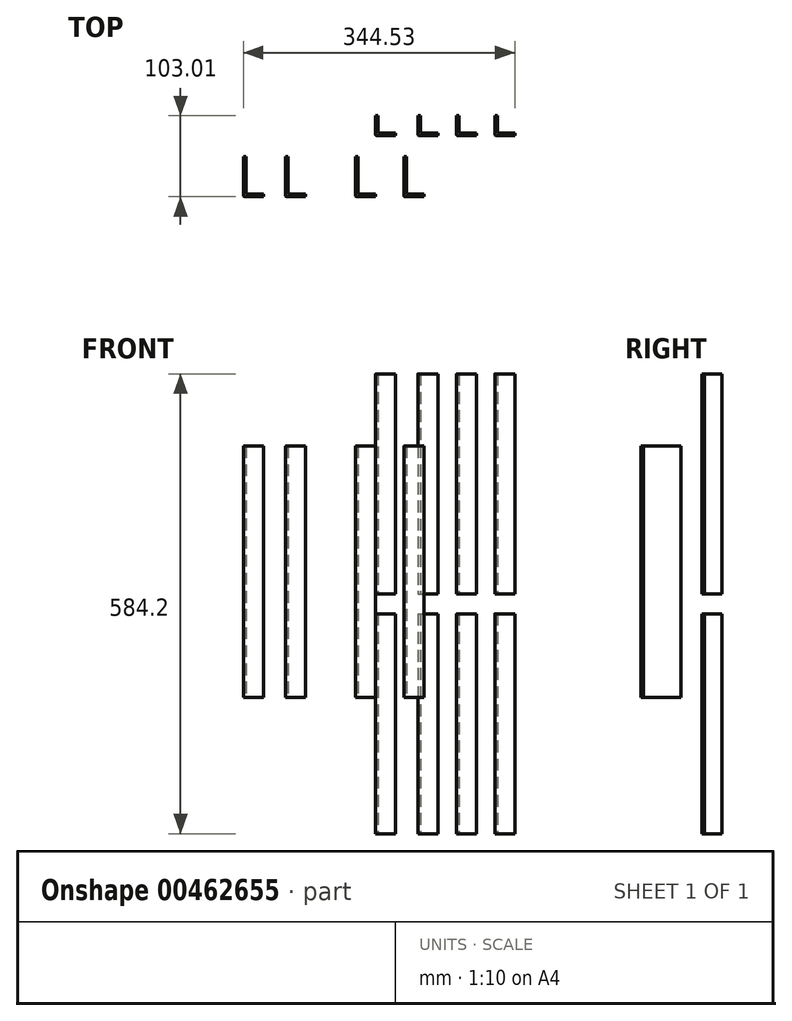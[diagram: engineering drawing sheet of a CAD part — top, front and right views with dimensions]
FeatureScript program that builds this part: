
annotation { "Feature Type Name" : "Feature", "Feature Type Description" : "" }
export const myFeature = defineFeature(function(context is Context, id is Id, definition is map)
    precondition{}
    {
        {
            var Q0;
            Q0=qCreatedBy(makeId("Top.planeOp"),FACE);
            var sketch = newSketch(context, id + "F0", { "sketchPlane" : qUnion([Q0])});
            skLineSegment(sketch, "E0", {"start": v(-52.96, 48.73) * mm, "end": v(-52.96, 24.92) * mm});
            skLineSegment(sketch, "E1", {"start": v(-51.37, 23.33) * mm, "end": v(-27.56, 23.33) * mm});
            skLineSegment(sketch, "E2", {"start": v(-27.56, 23.33) * mm, "end": v(-27.56, 26.5) * mm});
            skLineSegment(sketch, "E3", {"start": v(-27.56, 26.5) * mm, "end": v(-49.79, 26.5) * mm});
            skLineSegment(sketch, "E4", {"start": v(-52.96, 48.73) * mm, "end": v(-49.79, 48.73) * mm});
            skLineSegment(sketch, "E5", {"start": v(-49.79, 48.73) * mm, "end": v(-49.79, 26.5) * mm});
            skPoint(sketch, "E6.visualSharp", {"position": v(-52.96, 48.73) * mm});
            skPoint(sketch, "E7.visualSharp", {"position": v(-52.96, 23.33) * mm});
            skArc(sketch, "E7.filletArc", {"start": v(-52.96, 24.92) * mm, "mid": v(-52.5, 23.8) * mm, "end": v(-51.37, 23.33) * mm});
            skSolve(sketch);
        }
        {
            var Q0;
            Q0=makeQuery(id+"F0.imprint","IMPRINT",FACE,{"disambiguationData":[TD([[makeQuery(id+"F0.imprint","IMPRINT",EDGE,{"derivedFrom":sQuery(id+"F0.wireOp",EDGE,"E0")}),1.0]])]});
            extrude(context, id + "F1", {"entities" : qUnion([Q0]), "depth" : 279.4 * mm, "symmetric" : true});
        }
        {
            var Q0;
            Q0=makeQuery(id+"F1.opExtrude","SWEPT_BODY",BODY,{"disambiguationData":[OSD([sQuery(id+"F0.wireOp",EDGE,"E0"),sQuery(id+"F0.wireOp",EDGE,"E1"),sQuery(id+"F0.wireOp",EDGE,"E2"),sQuery(id+"F0.wireOp",EDGE,"E3"),sQuery(id+"F0.wireOp",EDGE,"E4"),sQuery(id+"F0.wireOp",EDGE,"E5"),sQuery(id+"F0.wireOp",EDGE,"E7.filletArc")])]});
            transform(context, id + "F2", {"entities" : qUnion([Q0]), "transformType" : TransformType.TRANSLATION_3D, "dx" : 53.6 * mm, "dy" : 0 * mm, "dz" : 0 * mm, "makeCopy" : true});
        }
        {
            var Q0;
            Q0=makeQuery(id+"F2.opPattern","COPY",BODY,{"derivedFrom":makeQuery(id+"F1.opExtrude","SWEPT_BODY",BODY,{"disambiguationData":[OSD([sQuery(id+"F0.wireOp",EDGE,"E0"),sQuery(id+"F0.wireOp",EDGE,"E1"),sQuery(id+"F0.wireOp",EDGE,"E2"),sQuery(id+"F0.wireOp",EDGE,"E3"),sQuery(id+"F0.wireOp",EDGE,"E4"),sQuery(id+"F0.wireOp",EDGE,"E5"),sQuery(id+"F0.wireOp",EDGE,"E7.filletArc")])]}),"instanceName":"1"});
            transform(context, id + "F3", {"entities" : qUnion([Q0]), "transformType" : TransformType.TRANSLATION_3D, "dx" : 49.28 * mm, "dy" : 0 * mm, "dz" : 0 * mm, "makeCopy" : true});
        }
        {
            var Q0;
            Q0=makeQuery(id+"F2.opPattern","COPY",BODY,{"derivedFrom":makeQuery(id+"F1.opExtrude","SWEPT_BODY",BODY,{"disambiguationData":[OSD([sQuery(id+"F0.wireOp",EDGE,"E0"),sQuery(id+"F0.wireOp",EDGE,"E1"),sQuery(id+"F0.wireOp",EDGE,"E2"),sQuery(id+"F0.wireOp",EDGE,"E3"),sQuery(id+"F0.wireOp",EDGE,"E4"),sQuery(id+"F0.wireOp",EDGE,"E5"),sQuery(id+"F0.wireOp",EDGE,"E7.filletArc")])]}),"instanceName":"1"});
            transform(context, id + "F4", {"entities" : qUnion([Q0]), "transformType" : TransformType.TRANSLATION_3D, "dx" : 97.8 * mm, "dy" : 0 * mm, "dz" : 0 * mm, "makeCopy" : true});
        }
        {
            var Q0;
            Q0=makeQuery(id+"F1.opExtrude","SWEPT_BODY",BODY,{"disambiguationData":[OSD([sQuery(id+"F0.wireOp",EDGE,"E0"),sQuery(id+"F0.wireOp",EDGE,"E1"),sQuery(id+"F0.wireOp",EDGE,"E2"),sQuery(id+"F0.wireOp",EDGE,"E3"),sQuery(id+"F0.wireOp",EDGE,"E4"),sQuery(id+"F0.wireOp",EDGE,"E5"),sQuery(id+"F0.wireOp",EDGE,"E7.filletArc")])]});
            var Q1;
            Q1=makeQuery(id+"F2.opPattern","COPY",BODY,{"derivedFrom":makeQuery(id+"F1.opExtrude","SWEPT_BODY",BODY,{"disambiguationData":[OSD([sQuery(id+"F0.wireOp",EDGE,"E0"),sQuery(id+"F0.wireOp",EDGE,"E1"),sQuery(id+"F0.wireOp",EDGE,"E2"),sQuery(id+"F0.wireOp",EDGE,"E3"),sQuery(id+"F0.wireOp",EDGE,"E4"),sQuery(id+"F0.wireOp",EDGE,"E5"),sQuery(id+"F0.wireOp",EDGE,"E7.filletArc")])]}),"instanceName":"1"});
            var Q2;
            Q2=makeQuery(id+"F4.opPattern","COPY",BODY,{"derivedFrom":makeQuery(id+"F2.opPattern","COPY",BODY,{"derivedFrom":makeQuery(id+"F1.opExtrude","SWEPT_BODY",BODY,{"disambiguationData":[OSD([sQuery(id+"F0.wireOp",EDGE,"E0"),sQuery(id+"F0.wireOp",EDGE,"E1"),sQuery(id+"F0.wireOp",EDGE,"E2"),sQuery(id+"F0.wireOp",EDGE,"E3"),sQuery(id+"F0.wireOp",EDGE,"E4"),sQuery(id+"F0.wireOp",EDGE,"E5"),sQuery(id+"F0.wireOp",EDGE,"E7.filletArc")])]}),"instanceName":"1"}),"instanceName":"1"});
            var Q3;
            Q3=makeQuery(id+"F3.opPattern","COPY",BODY,{"derivedFrom":makeQuery(id+"F2.opPattern","COPY",BODY,{"derivedFrom":makeQuery(id+"F1.opExtrude","SWEPT_BODY",BODY,{"disambiguationData":[OSD([sQuery(id+"F0.wireOp",EDGE,"E0"),sQuery(id+"F0.wireOp",EDGE,"E1"),sQuery(id+"F0.wireOp",EDGE,"E2"),sQuery(id+"F0.wireOp",EDGE,"E3"),sQuery(id+"F0.wireOp",EDGE,"E4"),sQuery(id+"F0.wireOp",EDGE,"E5"),sQuery(id+"F0.wireOp",EDGE,"E7.filletArc")])]}),"instanceName":"1"}),"instanceName":"1"});
            transform(context, id + "F5", {"entities" : qUnion([Q0, Q1, Q2, Q3]), "transformType" : TransformType.TRANSLATION_3D, "dx" : 0 * mm, "dy" : 0 * mm, "dz" : -193.3 * mm, "makeCopy" : false});
        }
        {
            var Q0;
            Q0=makeQuery(id+"F1.opExtrude","SWEPT_BODY",BODY,{"disambiguationData":[OSD([sQuery(id+"F0.wireOp",EDGE,"E0"),sQuery(id+"F0.wireOp",EDGE,"E1"),sQuery(id+"F0.wireOp",EDGE,"E2"),sQuery(id+"F0.wireOp",EDGE,"E3"),sQuery(id+"F0.wireOp",EDGE,"E4"),sQuery(id+"F0.wireOp",EDGE,"E5"),sQuery(id+"F0.wireOp",EDGE,"E7.filletArc")])]});
            var Q1;
            Q1=makeQuery(id+"F2.opPattern","COPY",BODY,{"derivedFrom":makeQuery(id+"F1.opExtrude","SWEPT_BODY",BODY,{"disambiguationData":[OSD([sQuery(id+"F0.wireOp",EDGE,"E0"),sQuery(id+"F0.wireOp",EDGE,"E1"),sQuery(id+"F0.wireOp",EDGE,"E2"),sQuery(id+"F0.wireOp",EDGE,"E3"),sQuery(id+"F0.wireOp",EDGE,"E4"),sQuery(id+"F0.wireOp",EDGE,"E5"),sQuery(id+"F0.wireOp",EDGE,"E7.filletArc")])]}),"instanceName":"1"});
            var Q2;
            Q2=makeQuery(id+"F3.opPattern","COPY",BODY,{"derivedFrom":makeQuery(id+"F2.opPattern","COPY",BODY,{"derivedFrom":makeQuery(id+"F1.opExtrude","SWEPT_BODY",BODY,{"disambiguationData":[OSD([sQuery(id+"F0.wireOp",EDGE,"E0"),sQuery(id+"F0.wireOp",EDGE,"E1"),sQuery(id+"F0.wireOp",EDGE,"E2"),sQuery(id+"F0.wireOp",EDGE,"E3"),sQuery(id+"F0.wireOp",EDGE,"E4"),sQuery(id+"F0.wireOp",EDGE,"E5"),sQuery(id+"F0.wireOp",EDGE,"E7.filletArc")])]}),"instanceName":"1"}),"instanceName":"1"});
            var Q3;
            Q3=makeQuery(id+"F4.opPattern","COPY",BODY,{"derivedFrom":makeQuery(id+"F2.opPattern","COPY",BODY,{"derivedFrom":makeQuery(id+"F1.opExtrude","SWEPT_BODY",BODY,{"disambiguationData":[OSD([sQuery(id+"F0.wireOp",EDGE,"E0"),sQuery(id+"F0.wireOp",EDGE,"E1"),sQuery(id+"F0.wireOp",EDGE,"E2"),sQuery(id+"F0.wireOp",EDGE,"E3"),sQuery(id+"F0.wireOp",EDGE,"E4"),sQuery(id+"F0.wireOp",EDGE,"E5"),sQuery(id+"F0.wireOp",EDGE,"E7.filletArc")])]}),"instanceName":"1"}),"instanceName":"1"});
            transform(context, id + "F6", {"entities" : qUnion([Q0, Q1, Q2, Q3]), "transformType" : TransformType.TRANSLATION_3D, "dx" : 0 * mm, "dy" : 0 * mm, "dz" : 304.8 * mm, "makeCopy" : true});
        }
        {
            var Q0;
            Q0=qCreatedBy(makeId("Top.planeOp"),FACE);
            var sketch = newSketch(context, id + "F7", { "sketchPlane" : qUnion([Q0])});
            skLineSegment(sketch, "E8", {"start": v(-78.47, -3.48) * mm, "end": v(-78.47, -52.68) * mm});
            skLineSegment(sketch, "E9", {"start": v(-76.87, -54.28) * mm, "end": v(-53.07, -54.28) * mm});
            skLineSegment(sketch, "E10", {"start": v(-53.07, -54.28) * mm, "end": v(-53.07, -51.1) * mm});
            skLineSegment(sketch, "E11", {"start": v(-53.07, -51.1) * mm, "end": v(-75.3, -51.1) * mm});
            skLineSegment(sketch, "E12", {"start": v(-78.47, -3.48) * mm, "end": v(-75.3, -3.48) * mm});
            skLineSegment(sketch, "E13", {"start": v(-75.3, -3.48) * mm, "end": v(-75.3, -51.1) * mm});
            skPoint(sketch, "E14.visualSharp", {"position": v(-78.47, -54.28) * mm});
            skArc(sketch, "E14.filletArc", {"start": v(-78.47, -52.68) * mm, "mid": v(-78, -53.81) * mm, "end": v(-76.87, -54.28) * mm});
            skSolve(sketch);
        }
        {
            var Q0;
            Q0=makeQuery(id+"F7.imprint","IMPRINT",FACE,{"disambiguationData":[TD([[makeQuery(id+"F7.imprint","IMPRINT",EDGE,{"derivedFrom":sQuery(id+"F7.wireOp",EDGE,"E8")}),1.0]])]});
            extrude(context, id + "F8", {"entities" : qUnion([Q0]), "depth" : 318.93 * mm, "symmetric" : true});
        }
        {
            var Q0;
            Q0=makeQuery(id+"F8.opExtrude","SWEPT_BODY",BODY,{"disambiguationData":[OSD([sQuery(id+"F7.wireOp",EDGE,"E8"),sQuery(id+"F7.wireOp",EDGE,"E9"),sQuery(id+"F7.wireOp",EDGE,"E10"),sQuery(id+"F7.wireOp",EDGE,"E11"),sQuery(id+"F7.wireOp",EDGE,"E12"),sQuery(id+"F7.wireOp",EDGE,"E13"),sQuery(id+"F7.wireOp",EDGE,"E14.filletArc")])]});
            transform(context, id + "F9", {"entities" : qUnion([Q0]), "transformType" : TransformType.TRANSLATION_3D, "dx" : 61.47 * mm, "dy" : 0 * mm, "dz" : 0 * mm, "makeCopy" : true});
        }
        {
            var Q0;
            Q0=makeQuery(id+"F8.opExtrude","SWEPT_BODY",BODY,{"disambiguationData":[OSD([sQuery(id+"F7.wireOp",EDGE,"E8"),sQuery(id+"F7.wireOp",EDGE,"E9"),sQuery(id+"F7.wireOp",EDGE,"E10"),sQuery(id+"F7.wireOp",EDGE,"E11"),sQuery(id+"F7.wireOp",EDGE,"E12"),sQuery(id+"F7.wireOp",EDGE,"E13"),sQuery(id+"F7.wireOp",EDGE,"E14.filletArc")])]});
            transform(context, id + "F10", {"entities" : qUnion([Q0]), "transformType" : TransformType.TRANSLATION_3D, "dx" : -88.9 * mm, "dy" : 0 * mm, "dz" : 0 * mm, "makeCopy" : true});
        }
        {
            var Q0;
            Q0=makeQuery(id+"F10.opPattern","COPY",BODY,{"derivedFrom":makeQuery(id+"F8.opExtrude","SWEPT_BODY",BODY,{"disambiguationData":[OSD([sQuery(id+"F7.wireOp",EDGE,"E8"),sQuery(id+"F7.wireOp",EDGE,"E9"),sQuery(id+"F7.wireOp",EDGE,"E10"),sQuery(id+"F7.wireOp",EDGE,"E11"),sQuery(id+"F7.wireOp",EDGE,"E12"),sQuery(id+"F7.wireOp",EDGE,"E13"),sQuery(id+"F7.wireOp",EDGE,"E14.filletArc")])]}),"instanceName":"1"});
            transform(context, id + "F11", {"entities" : qUnion([Q0]), "transformType" : TransformType.TRANSLATION_3D, "dx" : -53.34 * mm, "dy" : 0 * mm, "dz" : 0 * mm, "makeCopy" : true});
        }
    });
